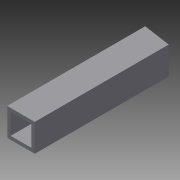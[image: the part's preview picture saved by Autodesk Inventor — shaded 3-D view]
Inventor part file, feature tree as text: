
AUTODESK INVENTOR PART (.ipt)
format: ipt  version: 2013 (Build 170138000, 138)  size: 83,456 bytes
history: native  units: in
note: dims shown in document units (in); Inventor stores cm internally (conversion verified against a paired STEP export)
features: extrude x2, sketch x2
ambient origin geometry x8: Origin, YZ Plane, XZ Plane, XY Plane, X Axis, Y Axis, Z Axis, Center Point
bodies: Solid1 (feature_tree)
feature tree (4):
  extrude  "Extrusion1"  Depth=1.0in
  extrude  "Extrusion2"  Depth=5.0in TaperAngle=0.0deg
  sketch  "Sketch1"  dims[d0=1.0in d1=1.0in]
  sketch  "Sketch2"  dims[d2=0.125in d3=5.0in d4=0.0in d5=0.0586in d6=5.0in d7=0.0in]
